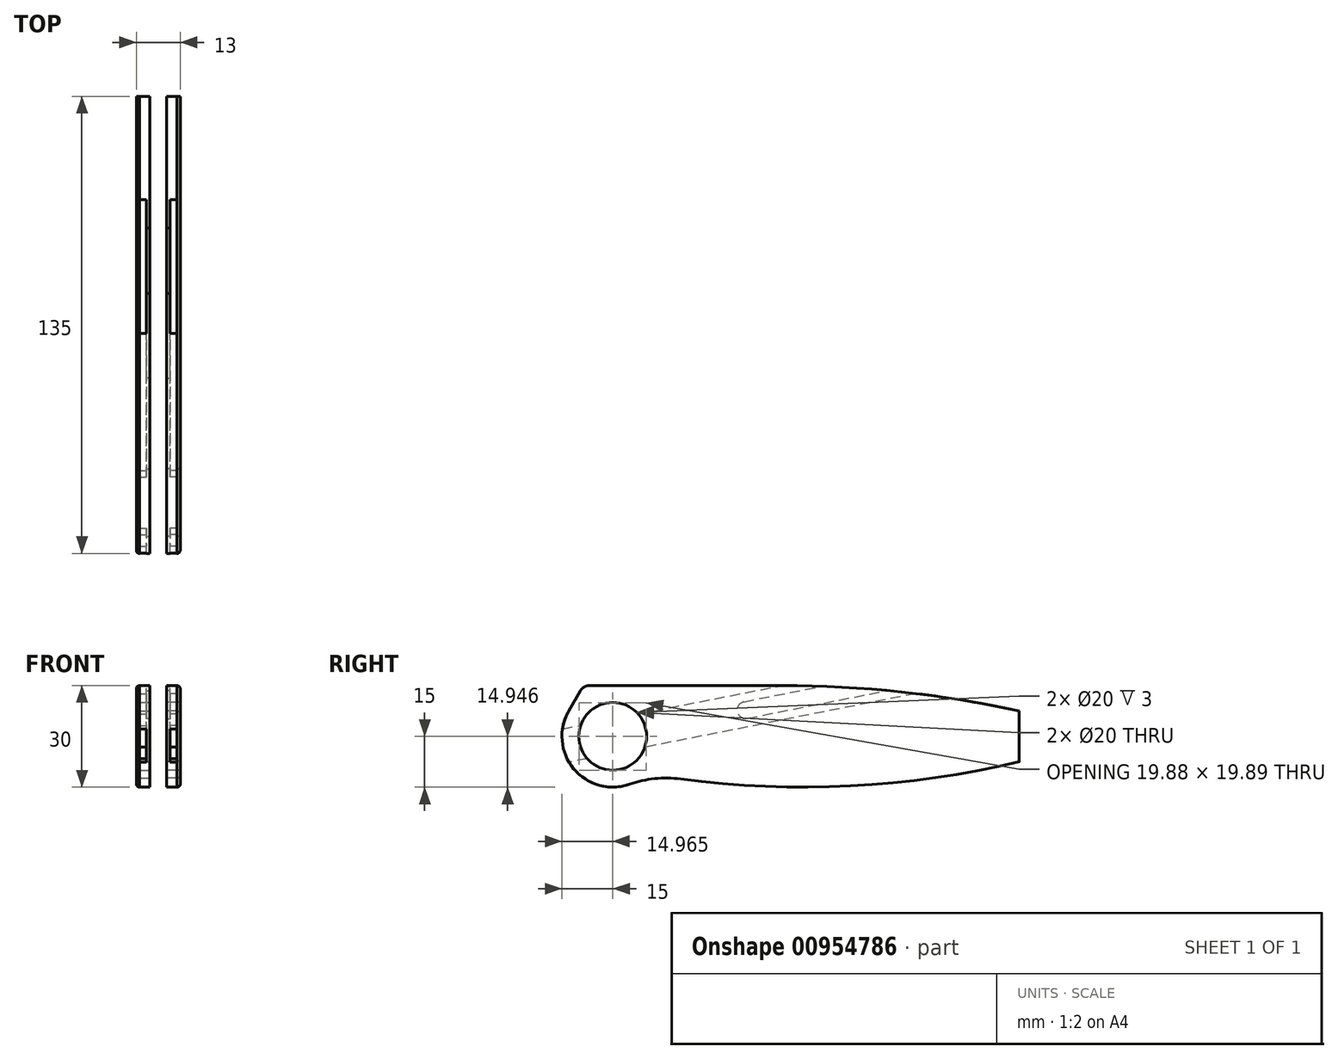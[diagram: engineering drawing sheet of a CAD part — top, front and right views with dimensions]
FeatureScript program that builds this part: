
annotation { "Feature Type Name" : "Feature", "Feature Type Description" : "" }
export const myFeature = defineFeature(function(context is Context, id is Id, definition is map)
    precondition{}
    {
        {
            var Q0;
            Q0=qCreatedBy(makeId("Right.planeOp"),FACE);
            cPlane(context, id + "F0", {"entities" : qUnion([Q0]), "cplaneType" : CPlaneType.OFFSET, "offset" : 2.5 * mm, "width" : 150 * mm, "height" : 150 * mm});
        }
        {
            var Q0;
            Q0=qCreatedBy(id+"F0.planeOp",FACE);
            var sketch = newSketch(context, id + "F1", { "sketchPlane" : qUnion([Q0])});
            skLineSegment(sketch, "E0", {"start": v(-26.34, 0) * mm, "end": v(120, 0) * mm, "construction": true});
            skLineSegment(sketch, "E1", {"start": v(0, 36.1) * mm, "end": v(0, -36.1) * mm, "construction": true});
            skArc(sketch, "E2", {"start": v(-13, 7.5) * mm, "mid": v(-11.54, -9.59) * mm, "end": v(5, -14.14) * mm});
            skArc(sketch, "E3", {"start": v(20, -12.58) * mm, "mid": v(12.4, -12.47) * mm, "end": v(5, -14.14) * mm});
            skArc(sketch, "E4", {"start": v(20, -12.58) * mm, "mid": v(70.23, -14.65) * mm, "end": v(120, -7.5) * mm});
            skLineSegment(sketch, "E5", {"start": v(120, -7.5) * mm, "end": v(120, 7.5) * mm});
            skLineSegment(sketch, "E6", {"start": v(-6.93, 15) * mm, "end": v(50, 15) * mm});
            skArc(sketch, "E7", {"start": v(50, 15) * mm, "mid": v(85.2, 13.12) * mm, "end": v(120, 7.5) * mm});
            skLineSegment(sketch, "E8", {"start": v(34.49, -15) * mm, "end": v(92.28, -15) * mm, "construction": true});
            skCircle(sketch, "E9", {"center": v(0, 0) * mm, "radius": 10 * mm});
            skArc(sketch, "E10", {"start": v(-6.93, 15) * mm, "mid": v(-8.43, 14.6) * mm, "end": v(-9.53, 13.5) * mm});
            skLineSegment(sketch, "E11", {"start": v(-13, 7.5) * mm, "end": v(-9.53, 13.5) * mm});
            skCircle(sketch, "E12", {"center": v(-13.57, 11.5) * mm, "radius": 2.5 * mm, "construction": true});
            skArc(sketch, "E13", {"start": v(-13.57, 11.5) * mm, "mid": v(-13.89, -11.11) * mm, "end": v(8.24, -15.76) * mm, "construction": true});
            skCircle(sketch, "E14", {"center": v(8.24, -15.76) * mm, "radius": 2.5 * mm, "construction": true});
            skSolve(sketch);
        }
        {
            var Q0;
            Q0=qSketchRegion(id+"F1",true);
            extrude(context, id + "F2", {"entities" : qUnion([Q0]), "depth" : 3 * mm, "offsetDistance" : 25 * mm});
        }
        {
            var Q0;
            Q0=makeQuery(id+"F2.opExtrude","CAP_FACE",FACE,{"disambiguationData":[OSD([sQuery(id+"F1.wireOp",EDGE,"E2"),sQuery(id+"F1.wireOp",EDGE,"E3"),sQuery(id+"F1.wireOp",EDGE,"E4"),sQuery(id+"F1.wireOp",EDGE,"E5"),sQuery(id+"F1.wireOp",EDGE,"E6"),sQuery(id+"F1.wireOp",EDGE,"E7"),sQuery(id+"F1.wireOp",EDGE,"E9"),sQuery(id+"F1.wireOp",EDGE,"E10"),sQuery(id+"F1.wireOp",EDGE,"E11")])],"isStart":false});
            var sketch = newSketch(context, id + "F3", { "sketchPlane" : qUnion([Q0])});
            skLineSegment(sketch, "E15", {"start": v(-25.74, 0) * mm, "end": v(50, 15) * mm});
            skLineSegment(sketch, "E16", {"start": v(50, 15) * mm, "end": v(101.47, 15) * mm});
            skLineSegment(sketch, "E17", {"start": v(101.47, 15) * mm, "end": v(-25.74, -10.2) * mm});
            skLineSegment(sketch, "E18", {"start": v(-25.74, -10.2) * mm, "end": v(-25.74, 0) * mm});
            skLineSegment(sketch, "E19", {"start": v(-0.97, 4.9) * mm, "end": v(0.97, -4.9) * mm, "construction": true});
            skSolve(sketch);
        }
        {
            var Q0;
            Q0=qSketchRegion(id+"F3",true);
            extrude(context, id + "F4", {"entities" : qUnion([Q0]), "operationType" : NewBodyOperationType.REMOVE, "oppositeDirection" : true, "depth" : 2 * mm, "offsetDistance" : 25 * mm});
        }
        {
            var Q0;
            {var subQ0=sQuery(id+"F3.wireOp",EDGE,"E15");var subQ1=sQuery(id+"F3.wireOp",EDGE,"E17");Q0=makeQuery(id+"F4.boolean.opBoolean","COPY",FACE,{"disambiguationData":[TD([makeQuery(id+"F2.opExtrude","SWEPT_FACE",FACE,{"disambiguationData":[OSD([sQuery(id+"F1.wireOp",EDGE,"E6")])]})])],"derivedFrom":makeQuery(id+"F4.opExtrude","CAP_FACE",FACE,{"disambiguationData":[OSD([subQ0,sQuery(id+"F3.wireOp",EDGE,"E16"),subQ1,sQuery(id+"F3.wireOp",EDGE,"E18")])],"isStart":false})});}
            var sketch = newSketch(context, id + "F5", { "sketchPlane" : qUnion([Q0])});
            skLineSegment(sketch, "E20", {"start": v(38.75, 10.22) * mm, "end": v(61.8, 14.79) * mm});
            skLineSegment(sketch, "E21", {"start": v(39.72, 5.32) * mm, "end": v(87.54, 14.79) * mm});
            skArc(sketch, "E22", {"start": v(38.75, 10.22) * mm, "mid": v(36.79, 7.29) * mm, "end": v(39.72, 5.32) * mm});
            skLineSegment(sketch, "E23", {"start": v(61.8, 14.79) * mm, "end": v(87.54, 14.79) * mm});
            skLineSegment(sketch, "E24", {"start": v(39.24, 7.77) * mm, "end": v(81.16, 16.07) * mm, "construction": true});
            skSolve(sketch);
        }
        {
            var Q0;
            Q0=qSketchRegion(id+"F5",true);
            extrude(context, id + "F6", {"entities" : qUnion([Q0]), "operationType" : NewBodyOperationType.REMOVE, "endBound" : BoundingType.THROUGH_ALL, "oppositeDirection" : true, "depth" : 25 * mm, "offsetDistance" : 25 * mm});
        }
        {
            var Q0;
            Q0=qSketchRegion(id+"F1",true);
            extrude(context, id + "F7", {"entities" : qUnion([Q0]), "depth" : 4 * mm, "offsetDistance" : 25 * mm, "hasSecondDirection" : true, "secondDirectionOppositeDirection" : false, "secondDirectionDepth" : 3 * mm});
        }
        {
            var Q0;
            Q0=makeQuery(id+"F7.opExtrude","CAP_EDGE",EDGE,{"disambiguationData":[OSD([sQuery(id+"F1.wireOp",EDGE,"E11")])],"isStart":false});
            fillet(context, id + "F8", {"entities" : qUnion([Q0]), "radius" : 1 * mm, "tangentPropagation" : true, "allowEdgeOverflow" : false});
        }
        {
            var Q0;
            Q0=makeQuery(id+"F2.opExtrude","SWEPT_BODY",BODY,{"disambiguationData":[OSD([sQuery(id+"F1.wireOp",EDGE,"E2"),sQuery(id+"F1.wireOp",EDGE,"E3"),sQuery(id+"F1.wireOp",EDGE,"E4"),sQuery(id+"F1.wireOp",EDGE,"E5"),sQuery(id+"F1.wireOp",EDGE,"E6"),sQuery(id+"F1.wireOp",EDGE,"E7"),sQuery(id+"F1.wireOp",EDGE,"E9")])]});
            var Q1;
            Q1=makeQuery(id+"F7.opExtrude","SWEPT_BODY",BODY,{"disambiguationData":[OSD([sQuery(id+"F1.wireOp",EDGE,"E2"),sQuery(id+"F1.wireOp",EDGE,"E3"),sQuery(id+"F1.wireOp",EDGE,"E4"),sQuery(id+"F1.wireOp",EDGE,"E5"),sQuery(id+"F1.wireOp",EDGE,"E6"),sQuery(id+"F1.wireOp",EDGE,"E7"),sQuery(id+"F1.wireOp",EDGE,"E9"),sQuery(id+"F1.wireOp",EDGE,"E10"),sQuery(id+"F1.wireOp",EDGE,"E11")])]});
            var Q2;
            Q2=qCreatedBy(makeId("Right.planeOp"),FACE);
            mirror(context, id + "F9", {"entities" : qUnion([Q0, Q1]), "mirrorPlane" : qUnion([Q2])});
        }
    });
